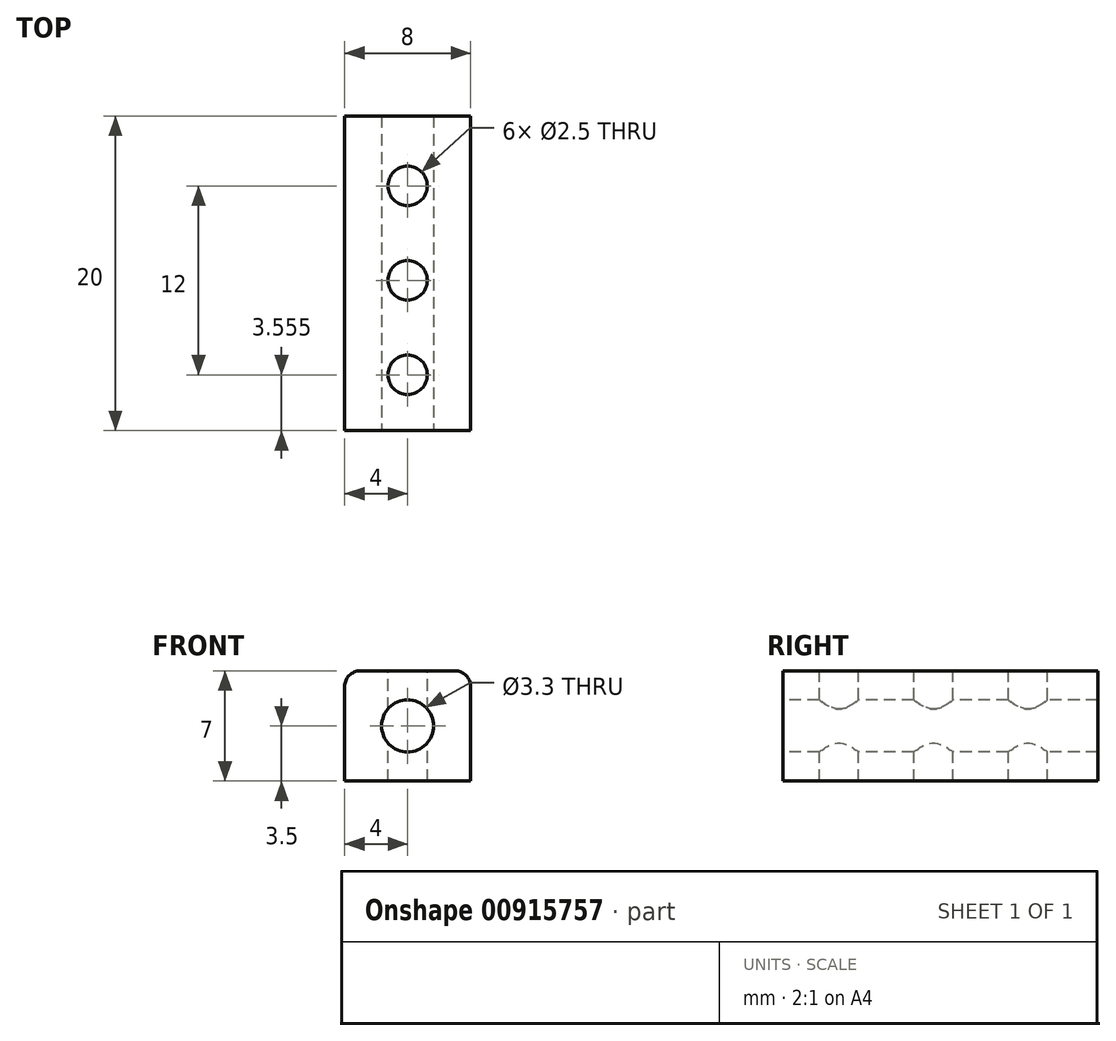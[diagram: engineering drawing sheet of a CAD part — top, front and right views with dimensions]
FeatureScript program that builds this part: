
annotation { "Feature Type Name" : "Feature", "Feature Type Description" : "" }
export const myFeature = defineFeature(function(context is Context, id is Id, definition is map)
    precondition{}
    {
        {
            var Q0;
            Q0=qCreatedBy(makeId("Front.planeOp"),FACE);
            var sketch = newSketch(context, id + "F0", { "sketchPlane" : qUnion([Q0])});
            skLineSegment(sketch, "E0.bottom", {"start": v(-4, 3.5) * mm, "end": v(4, 3.5) * mm});
            skLineSegment(sketch, "E0.top", {"start": v(-4, -3.5) * mm, "end": v(4, -3.5) * mm});
            skLineSegment(sketch, "E0.left", {"start": v(-4, 3.5) * mm, "end": v(-4, -3.5) * mm});
            skLineSegment(sketch, "E0.right", {"start": v(4, 3.5) * mm, "end": v(4, -3.5) * mm});
            skPoint(sketch, "E0.middle", {"position": v(0, 0) * mm});
            skCircle(sketch, "E1", {"center": v(0, 0) * mm, "radius": 1.65 * mm});
            skSolve(sketch);
        }
        {
            var Q0;
            Q0=makeQuery(id+"F0.imprint","IMPRINT",FACE,{"disambiguationData":[TD([[makeQuery(id+"F0.imprint","IMPRINT",EDGE,{"derivedFrom":sQuery(id+"F0.wireOp",EDGE,"E0.bottom")}),-1.0]])]});
            extrude(context, id + "F1", {"entities" : qUnion([Q0]), "oppositeDirection" : true, "depth" : 20 * mm, "offsetDistance" : 25 * mm});
        }
        {
            var Q0;
            Q0=makeQuery(id+"F1.opExtrude","SWEPT_FACE",FACE,{"disambiguationData":[OSD([sQuery(id+"F0.wireOp",EDGE,"E0.bottom")])]});
            var sketch = newSketch(context, id + "F2", { "sketchPlane" : qUnion([Q0])});
            skCircle(sketch, "E2", {"center": v(0, 15.55) * mm, "radius": 1.25 * mm});
            skCircle(sketch, "E3", {"center": v(0, 9.55) * mm, "radius": 1.25 * mm});
            skCircle(sketch, "E4", {"center": v(0, 3.55) * mm, "radius": 1.25 * mm});
            skSolve(sketch);
        }
        {
            var Q0;
            Q0=makeQuery(id+"F2.imprint","IMPRINT",FACE,{"disambiguationData":[TD([[makeQuery(id+"F2.imprint","IMPRINT",EDGE,{"derivedFrom":sQuery(id+"F2.wireOp",EDGE,"E2")}),1.0]])]});
            var Q1;
            Q1=makeQuery(id+"F2.imprint","IMPRINT",FACE,{"disambiguationData":[TD([[makeQuery(id+"F2.imprint","IMPRINT",EDGE,{"derivedFrom":sQuery(id+"F2.wireOp",EDGE,"E3")}),1.0]])]});
            var Q2;
            Q2=makeQuery(id+"F2.imprint","IMPRINT",FACE,{"disambiguationData":[TD([[makeQuery(id+"F2.imprint","IMPRINT",EDGE,{"derivedFrom":sQuery(id+"F2.wireOp",EDGE,"E4")}),1.0]])]});
            extrude(context, id + "F3", {"entities" : qUnion([Q0, Q1, Q2]), "operationType" : NewBodyOperationType.REMOVE, "endBound" : BoundingType.THROUGH_ALL, "oppositeDirection" : true, "depth" : 25 * mm, "offsetDistance" : 25 * mm});
        }
        {
            var Q0;
            Q0=makeQuery(id+"F1.opExtrude","SWEPT_EDGE",EDGE,{"disambiguationData":[OSD([sQuery(id+"F0.wireOp",EDGE,"E0.bottom"),sQuery(id+"F0.wireOp",EDGE,"E0.right")])]});
            var Q1;
            Q1=makeQuery(id+"F1.opExtrude","SWEPT_EDGE",EDGE,{"disambiguationData":[OSD([sQuery(id+"F0.wireOp",EDGE,"E0.bottom"),sQuery(id+"F0.wireOp",EDGE,"E0.left")])]});
            fillet(context, id + "F4", {"entities" : qUnion([Q0, Q1]), "radius" : 1 * mm, "allowEdgeOverflow" : false});
        }
    });
